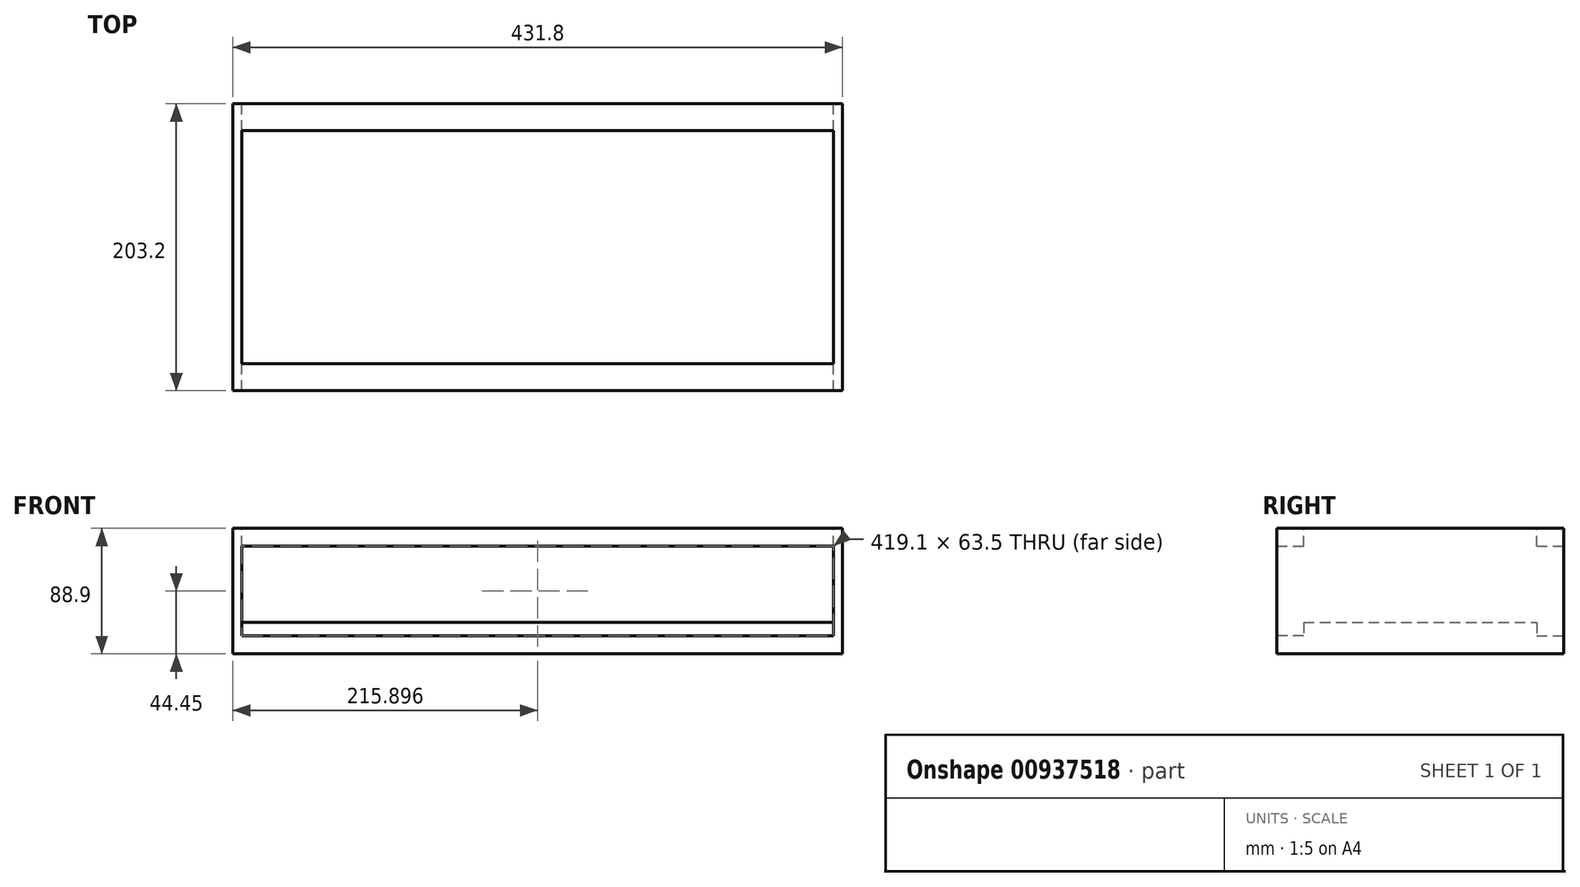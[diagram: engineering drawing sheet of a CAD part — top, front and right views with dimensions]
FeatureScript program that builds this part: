
annotation { "Feature Type Name" : "Feature", "Feature Type Description" : "" }
export const myFeature = defineFeature(function(context is Context, id is Id, definition is map)
    precondition{}
    {
        {
            var Q0;
            Q0=qCreatedBy(makeId("Top.planeOp"),FACE);
            var sketch = newSketch(context, id + "F0", { "sketchPlane" : qUnion([Q0])});
            skLineSegment(sketch, "E0.bottom", {"start": v(-175.13, 112.38) * mm, "end": v(256.67, 112.38) * mm});
            skLineSegment(sketch, "E0.top", {"start": v(-175.13, -90.82) * mm, "end": v(256.67, -90.82) * mm});
            skLineSegment(sketch, "E0.left", {"start": v(-175.13, 112.38) * mm, "end": v(-175.13, -90.82) * mm});
            skLineSegment(sketch, "E0.right", {"start": v(256.67, 112.38) * mm, "end": v(256.67, -90.82) * mm});
            skSolve(sketch);
        }
        {
            var Q0;
            Q0=makeQuery(id+"F0.imprint","IMPRINT",FACE,{"disambiguationData":[TD([[makeQuery(id+"F0.imprint","IMPRINT",EDGE,{"derivedFrom":sQuery(id+"F0.wireOp",EDGE,"E0.bottom")}),-1.0]])]});
            extrude(context, id + "F1", {"entities" : qUnion([Q0]), "depth" : 88.9 * mm, "offsetDistance" : 25.4 * mm});
        }
        {
            var Q0;
            Q0=makeQuery(id+"F1.opExtrude","SWEPT_FACE",FACE,{"disambiguationData":[OSD([sQuery(id+"F0.wireOp",EDGE,"E0.bottom")])]});
            var sketch = newSketch(context, id + "F2", { "sketchPlane" : qUnion([Q0])});
            skLineSegment(sketch, "E1.bottom", {"start": v(168.78, 22.23) * mm, "end": v(-250.32, 22.22) * mm});
            skLineSegment(sketch, "E1.top", {"start": v(168.78, 76.2) * mm, "end": v(-250.32, 76.2) * mm});
            skLineSegment(sketch, "E1.left", {"start": v(168.78, 22.23) * mm, "end": v(168.78, 76.2) * mm});
            skLineSegment(sketch, "E1.right", {"start": v(-250.32, 22.22) * mm, "end": v(-250.32, 76.2) * mm});
            skPoint(sketch, "E1.middle", {"position": v(-40.77, 49.21) * mm});
            skSolve(sketch);
        }
        {
            var Q0;
            Q0=makeQuery(id+"F2.imprint","IMPRINT",FACE,{"disambiguationData":[TD([[makeQuery(id+"F2.imprint","IMPRINT",EDGE,{"derivedFrom":sQuery(id+"F2.wireOp",EDGE,"E1.bottom")}),-1.0]])]});
            var Q1;
            Q1=makeQuery(id+"F1.opExtrude","SWEPT_FACE",FACE,{"disambiguationData":[OSD([sQuery(id+"F0.wireOp",EDGE,"E0.top")])]});
            extrude(context, id + "F3", {"entities" : qUnion([Q0]), "operationType" : NewBodyOperationType.REMOVE, "endBound" : BoundingType.UP_TO_SURFACE, "oppositeDirection" : true, "depth" : 25.4 * mm, "endBoundEntityFace" : qUnion([Q1]), "offsetDistance" : 25.4 * mm});
        }
        {
            var Q0;
            Q0=makeQuery(id+"F1.opExtrude","CAP_FACE",FACE,{"disambiguationData":[OSD([sQuery(id+"F0.wireOp",EDGE,"E0.bottom"),sQuery(id+"F0.wireOp",EDGE,"E0.top"),sQuery(id+"F0.wireOp",EDGE,"E0.left"),sQuery(id+"F0.wireOp",EDGE,"E0.right")])],"isStart":false});
            var sketch = newSketch(context, id + "F4", { "sketchPlane" : qUnion([Q0])});
            skLineSegment(sketch, "E2", {"start": v(-175.13, 10.78) * mm, "end": v(256.67, 10.78) * mm, "construction": true});
            skLineSegment(sketch, "E3", {"start": v(40.77, 112.38) * mm, "end": v(40.77, -90.82) * mm, "construction": true});
            skLineSegment(sketch, "E4.bottom", {"start": v(-168.78, 93.33) * mm, "end": v(250.32, 93.33) * mm});
            skLineSegment(sketch, "E4.top", {"start": v(-168.78, -71.77) * mm, "end": v(250.32, -71.77) * mm});
            skLineSegment(sketch, "E4.left", {"start": v(-168.78, 93.33) * mm, "end": v(-168.78, -71.77) * mm});
            skLineSegment(sketch, "E4.right", {"start": v(250.32, 93.33) * mm, "end": v(250.32, -71.77) * mm});
            skPoint(sketch, "E4.middle", {"position": v(40.77, 10.78) * mm});
            skSolve(sketch);
        }
        {
            var Q0;
            Q0=makeQuery(id+"F4.imprint","IMPRINT",FACE,{"disambiguationData":[TD([[makeQuery(id+"F4.imprint","IMPRINT",EDGE,{"derivedFrom":sQuery(id+"F4.wireOp",EDGE,"E4.bottom")}),-1.0]])]});
            var Q1;
            Q1=makeQuery(id+"F3.boolean.opBoolean","COPY",FACE,{"derivedFrom":makeQuery(id+"F3.opExtrude","SWEPT_FACE",FACE,{"disambiguationData":[OSD([sQuery(id+"F2.wireOp",EDGE,"E1.top")])]})});
            extrude(context, id + "F5", {"entities" : qUnion([Q0]), "operationType" : NewBodyOperationType.REMOVE, "endBound" : BoundingType.UP_TO_SURFACE, "oppositeDirection" : true, "depth" : 25.4 * mm, "endBoundEntityFace" : qUnion([Q1]), "offsetDistance" : 25.4 * mm});
        }
        {
            var Q0;
            Q0=makeQuery(id+"F1.opExtrude","SWEPT_FACE",FACE,{"disambiguationData":[OSD([sQuery(id+"F0.wireOp",EDGE,"E0.bottom")])]});
            var sketch = newSketch(context, id + "F6", { "sketchPlane" : qUnion([Q0])});
            skLineSegment(sketch, "E5.bottom", {"start": v(-250.32, 22.22) * mm, "end": v(168.78, 22.22) * mm});
            skLineSegment(sketch, "E5.top", {"start": v(-250.32, 12.7) * mm, "end": v(168.78, 12.7) * mm});
            skLineSegment(sketch, "E5.left", {"start": v(-250.32, 22.22) * mm, "end": v(-250.32, 12.7) * mm});
            skLineSegment(sketch, "E5.right", {"start": v(168.78, 22.22) * mm, "end": v(168.78, 12.7) * mm});
            skSolve(sketch);
        }
        {
            var Q0;
            Q0=makeQuery(id+"F6.imprint","IMPRINT",FACE,{"disambiguationData":[TD([[makeQuery(id+"F6.imprint","IMPRINT",EDGE,{"derivedFrom":sQuery(id+"F6.wireOp",EDGE,"E5.bottom")}),1.0]])]});
            extrude(context, id + "F7", {"entities" : qUnion([Q0]), "operationType" : NewBodyOperationType.REMOVE, "oppositeDirection" : true, "depth" : 19.05 * mm, "offsetDistance" : 25.4 * mm});
        }
        {
            var Q0;
            Q0=makeQuery(id+"F1.opExtrude","SWEPT_FACE",FACE,{"disambiguationData":[OSD([sQuery(id+"F0.wireOp",EDGE,"E0.top")])]});
            var sketch = newSketch(context, id + "F8", { "sketchPlane" : qUnion([Q0])});
            skLineSegment(sketch, "E6.bottom", {"start": v(-168.78, 22.23) * mm, "end": v(250.32, 22.23) * mm});
            skLineSegment(sketch, "E6.top", {"start": v(-168.78, 12.7) * mm, "end": v(250.32, 12.7) * mm});
            skLineSegment(sketch, "E6.left", {"start": v(-168.78, 22.23) * mm, "end": v(-168.78, 12.7) * mm});
            skLineSegment(sketch, "E6.right", {"start": v(250.32, 22.23) * mm, "end": v(250.32, 12.7) * mm});
            skSolve(sketch);
        }
        {
            var Q0;
            Q0=makeQuery(id+"F8.imprint","IMPRINT",FACE,{"disambiguationData":[TD([[makeQuery(id+"F8.imprint","IMPRINT",EDGE,{"derivedFrom":sQuery(id+"F8.wireOp",EDGE,"E6.bottom")}),1.0]])]});
            extrude(context, id + "F9", {"entities" : qUnion([Q0]), "operationType" : NewBodyOperationType.REMOVE, "oppositeDirection" : true, "depth" : 19.05 * mm, "offsetDistance" : 25.4 * mm});
        }
    });
